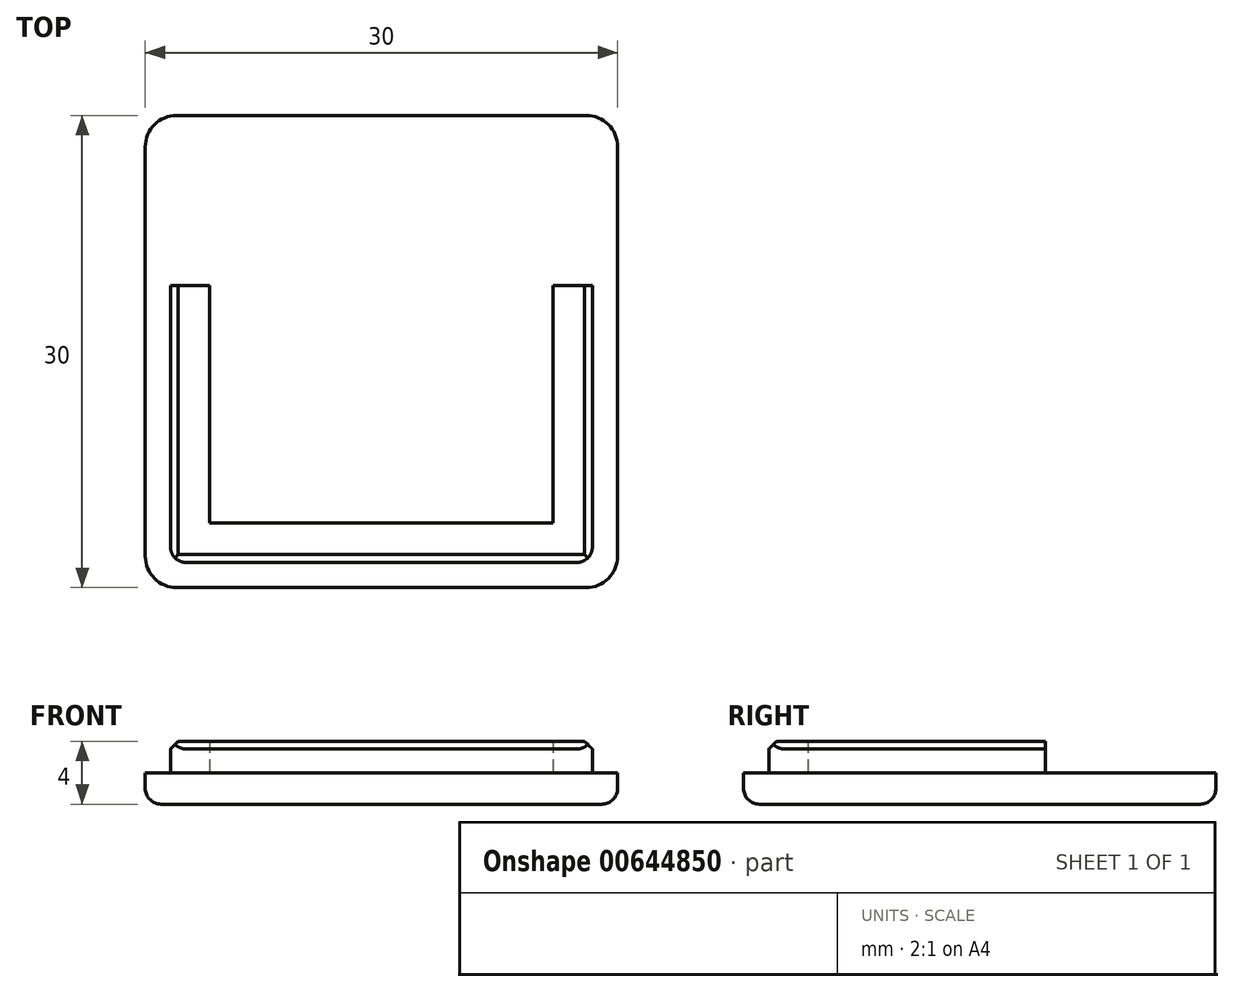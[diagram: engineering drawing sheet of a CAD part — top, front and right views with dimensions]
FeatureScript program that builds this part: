
annotation { "Feature Type Name" : "Feature", "Feature Type Description" : "" }
export const myFeature = defineFeature(function(context is Context, id is Id, definition is map)
    precondition{}
    {
        {
            var Q0;
            Q0=qCreatedBy(makeId("Top.planeOp"),FACE);
            var sketch = newSketch(context, id + "F0", { "sketchPlane" : qUnion([Q0])});
            skLineSegment(sketch, "E0.bottom", {"start": v(15, 15) * mm, "end": v(-15, 15) * mm});
            skLineSegment(sketch, "E0.top", {"start": v(15, -15) * mm, "end": v(-15, -15) * mm});
            skLineSegment(sketch, "E0.left", {"start": v(15, 15) * mm, "end": v(15, -15) * mm});
            skLineSegment(sketch, "E0.right", {"start": v(-15, 15) * mm, "end": v(-15, -15) * mm});
            skPoint(sketch, "E0.middle", {"position": v(0, 0) * mm});
            skLineSegment(sketch, "E1.bottom", {"start": v(13.4, 13.4) * mm, "end": v(-13.4, 13.4) * mm});
            skLineSegment(sketch, "E1.top", {"start": v(13.4, -13.4) * mm, "end": v(-13.4, -13.4) * mm});
            skLineSegment(sketch, "E1.left", {"start": v(13.4, 13.4) * mm, "end": v(13.4, -13.4) * mm});
            skLineSegment(sketch, "E1.right", {"start": v(-13.4, 13.4) * mm, "end": v(-13.4, -13.4) * mm});
            skLineSegment(sketch, "E2.top", {"start": v(10.9, -10.9) * mm, "end": v(-10.9, -10.9) * mm});
            skPoint(sketch, "E3.centerSnap0", {"position": v(0, 15) * mm});
            skLineSegment(sketch, "E4", {"start": v(-10.9, -10.9) * mm, "end": v(-10.9, 4.18) * mm});
            skLineSegment(sketch, "E5", {"start": v(-10.9, 4.18) * mm, "end": v(-13.4, 4.18) * mm});
            skLineSegment(sketch, "E6.MirrorCS", {"start": v(10.9, -10.9) * mm, "end": v(10.9, 4.18) * mm});
            skLineSegment(sketch, "E7.MirrorCS", {"start": v(10.9, 4.18) * mm, "end": v(13.4, 4.18) * mm});
            skSolve(sketch);
        }
        {
            var Q0;
            Q0 = qSketchRegion(id + "F0", true);
            var Q1;
            {var subQ1=sQuery(id+"F0.wireOp",EDGE,"E1.bottom");Q1=makeQuery(id+"F0.imprint","IMPRINT",FACE,{"disambiguationData":[TD([[makeQuery(id+"F0.imprint","IMPRINT",EDGE,{"derivedFrom":subQ1}),1.0]])]});}
            var Q2;
            {var subQ1=sQuery(id+"F0.wireOp",EDGE,"E1.top");Q2=makeQuery(id+"F0.imprint","IMPRINT",FACE,{"disambiguationData":[TD([[makeQuery(id+"F0.imprint","IMPRINT",EDGE,{"derivedFrom":subQ1}),-1.0]])]});}
            extrude(context, id + "F1", {"entities" : qUnion([Q0, Q1, Q2]), "depth" : 2 * mm, "offsetDistance" : 25 * mm});
        }
        {
            var Q0;
            {var subQ1=sQuery(id+"F0.wireOp",EDGE,"E1.top");Q0=makeQuery(id+"F0.imprint","IMPRINT",FACE,{"disambiguationData":[TD([[makeQuery(id+"F0.imprint","IMPRINT",EDGE,{"derivedFrom":subQ1}),-1.0]])]});}
            extrude(context, id + "F2", {"entities" : qUnion([Q0]), "operationType" : NewBodyOperationType.ADD, "depth" : 4 * mm, "offsetDistance" : 25 * mm});
        }
        {
            var Q0;
            Q0=makeQuery(id+"F1.opExtrude","SWEPT_EDGE",EDGE,{"disambiguationData":[OSD([sQuery(id+"F0.wireOp",EDGE,"E0.top"),sQuery(id+"F0.wireOp",EDGE,"E0.right")])]});
            var Q1;
            Q1=makeQuery(id+"F1.opExtrude","SWEPT_EDGE",EDGE,{"disambiguationData":[OSD([sQuery(id+"F0.wireOp",EDGE,"E0.bottom"),sQuery(id+"F0.wireOp",EDGE,"E0.right")])]});
            var Q2;
            Q2=makeQuery(id+"F1.opExtrude","SWEPT_EDGE",EDGE,{"disambiguationData":[OSD([sQuery(id+"F0.wireOp",EDGE,"E0.bottom"),sQuery(id+"F0.wireOp",EDGE,"E0.left")])]});
            var Q3;
            Q3=makeQuery(id+"F1.opExtrude","SWEPT_EDGE",EDGE,{"disambiguationData":[OSD([sQuery(id+"F0.wireOp",EDGE,"E0.top"),sQuery(id+"F0.wireOp",EDGE,"E0.left")])]});
            fillet(context, id + "F3", {"entities" : qUnion([Q0, Q1, Q2, Q3]), "radius" : 2 * mm, "tangentPropagation" : true, "allowEdgeOverflow" : false});
        }
        {
            var Q0;
            Q0=makeQuery(id+"F2.opExtrude","CAP_EDGE",EDGE,{"disambiguationData":[OSD([sQuery(id+"F0.wireOp",EDGE,"E1.left")])],"isStart":false});
            var Q1;
            Q1=makeQuery(id+"F2.opExtrude","CAP_EDGE",EDGE,{"disambiguationData":[OSD([sQuery(id+"F0.wireOp",EDGE,"E1.top")])],"isStart":false});
            var Q2;
            Q2=makeQuery(id+"F2.opExtrude","CAP_EDGE",EDGE,{"disambiguationData":[OSD([sQuery(id+"F0.wireOp",EDGE,"E1.right")])],"isStart":false});
            chamfer(context, id + "F4", {"entities" : qUnion([Q0, Q1, Q2]), "width" : .5 * mm, "tangentPropagation" : true});
        }
        {
            var Q0;
            Q0=makeQuery(id+"F1.opExtrude","CAP_EDGE",EDGE,{"disambiguationData":[OSD([sQuery(id+"F0.wireOp",EDGE,"E0.bottom")])],"isStart":true});
            fillet(context, id + "F5", {"entities" : qUnion([Q0]), "radius" : 1 * mm, "tangentPropagation" : true, "allowEdgeOverflow" : false});
        }
        {
            var Q0;
            Q0=makeQuery(id+"F2.opExtrude","SWEPT_EDGE",EDGE,{"disambiguationData":[OSD([sQuery(id+"F0.wireOp",EDGE,"E1.top"),sQuery(id+"F0.wireOp",EDGE,"E1.left")])]});
            var Q1;
            Q1=makeQuery(id+"F2.opExtrude","SWEPT_EDGE",EDGE,{"disambiguationData":[OSD([sQuery(id+"F0.wireOp",EDGE,"E1.top"),sQuery(id+"F0.wireOp",EDGE,"E1.right")])]});
            fillet(context, id + "F6", {"entities" : qUnion([Q0, Q1]), "radius" : 1 * mm, "tangentPropagation" : true, "allowEdgeOverflow" : false});
        }
    });
